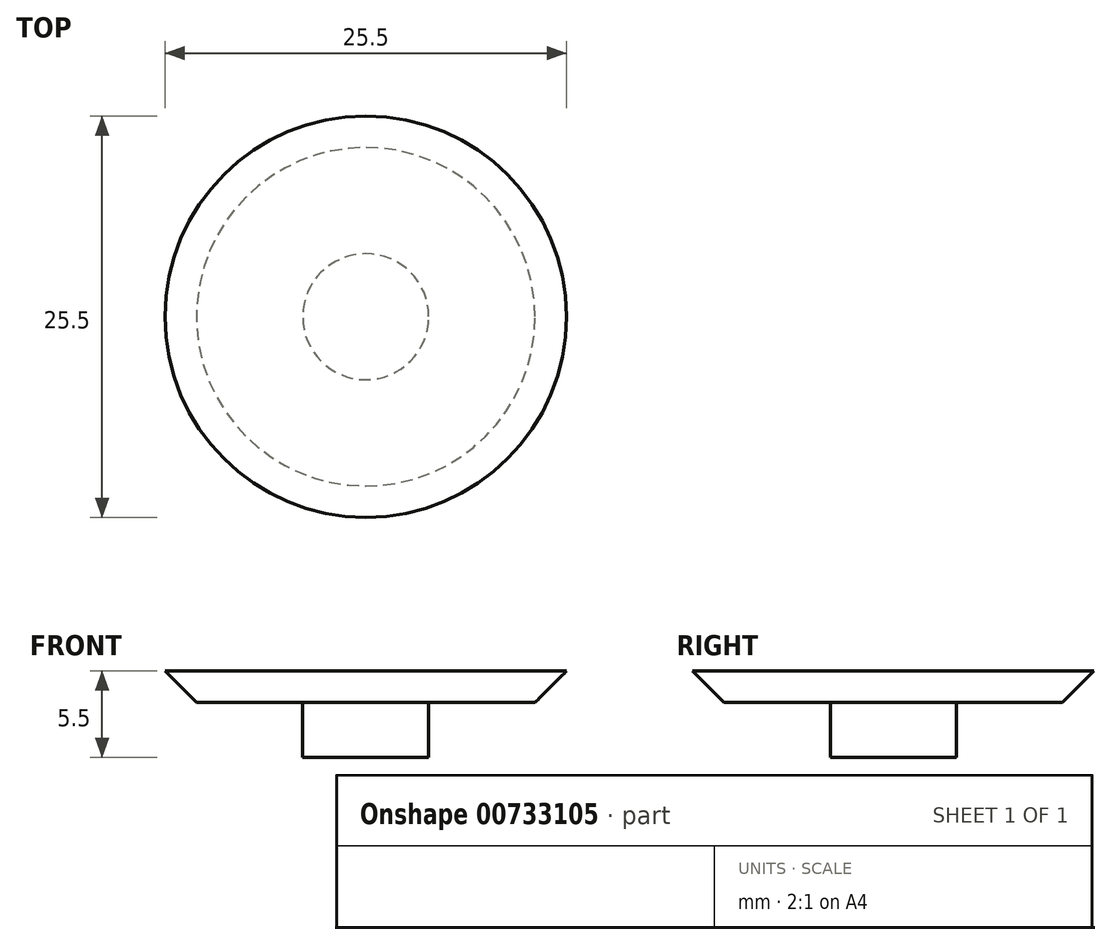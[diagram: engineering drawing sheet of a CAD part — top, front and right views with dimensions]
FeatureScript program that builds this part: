
annotation { "Feature Type Name" : "Feature", "Feature Type Description" : "" }
export const myFeature = defineFeature(function(context is Context, id is Id, definition is map)
    precondition{}
    {
        {
            var Q0;
            Q0=qCreatedBy(makeId("Top.planeOp"),FACE);
            var sketch = newSketch(context, id + "F0", { "sketchPlane" : qUnion([Q0])});
            skCircle(sketch, "E0", {"center": v(0, 0) * mm, "radius": 12.75 * mm});
            skSolve(sketch);
        }
        {
            var Q0;
            Q0 = qSketchRegion(id + "F0", true);
            extrude(context, id + "F1", {"entities" : qUnion([Q0]), "depth" : 2 * mm, "offsetDistance" : 25 * mm});
        }
        {
            var Q0;
            Q0=makeQuery(id+"F1.opExtrude","CAP_EDGE",EDGE,{"disambiguationData":[OSD([sQuery(id+"F0.wireOp",EDGE,"E0")])],"isStart":true});
            chamfer(context, id + "F2", {"entities" : qUnion([Q0]), "width" : 2 * mm, "tangentPropagation" : true});
        }
        {
            var Q0;
            Q0=makeQuery(id+"F1.opExtrude","CAP_FACE",FACE,{"disambiguationData":[OSD([sQuery(id+"F0.wireOp",EDGE,"E0")])],"isStart":true});
            var sketch = newSketch(context, id + "F3", { "sketchPlane" : qUnion([Q0])});
            skCircle(sketch, "E1", {"center": v(0, 0) * mm, "radius": 4 * mm});
            skSolve(sketch);
        }
        {
            var Q0;
            Q0=makeQuery(id+"F3.imprint","IMPRINT",FACE,{"disambiguationData":[TD([[makeQuery(id+"F3.imprint","IMPRINT",EDGE,{"derivedFrom":sQuery(id+"F3.wireOp",EDGE,"E1")}),1.0]])]});
            extrude(context, id + "F4", {"entities" : qUnion([Q0]), "operationType" : NewBodyOperationType.ADD, "depth" : 3.5 * mm, "offsetDistance" : 25 * mm});
        }
    });
